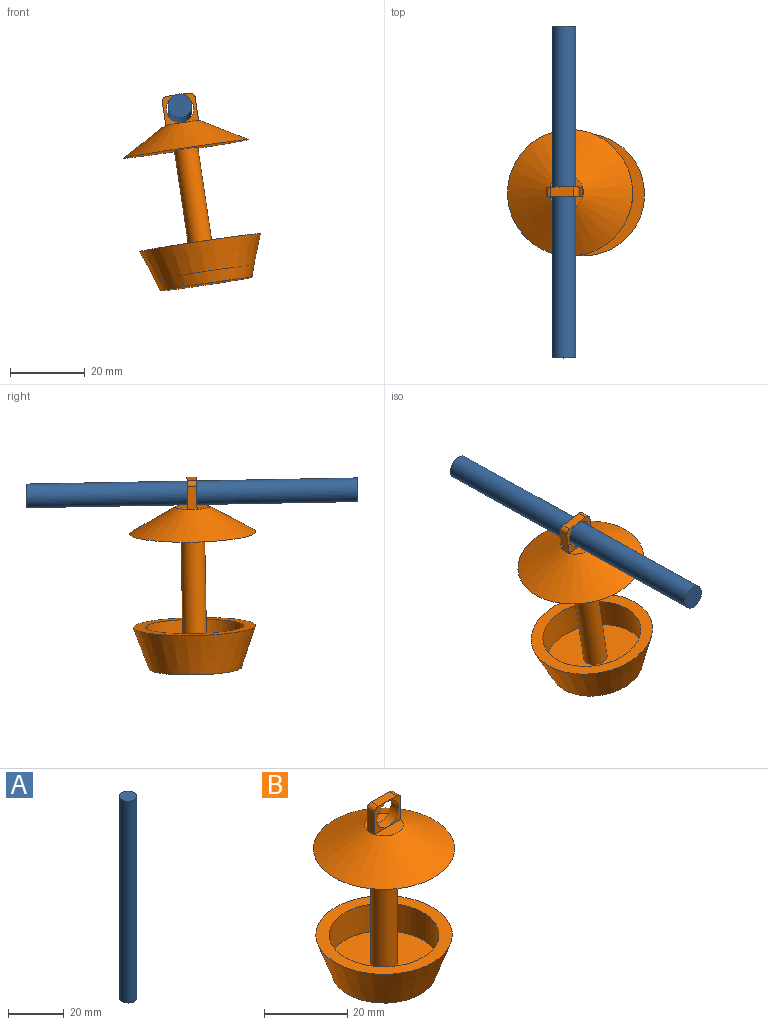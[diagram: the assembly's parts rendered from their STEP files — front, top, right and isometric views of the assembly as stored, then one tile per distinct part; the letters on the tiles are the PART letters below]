
ASSEMBLY  parts=2 mates=1
PART A: 3 faces, bbox 6.4x6.4x88.9 mm
  f0: cylinder r=3.17mm len=88.9mm, axis (0,0,-1), area 1773.5mm2, adj f1,f2
  f1: plane 6.35x6.35mm, normal (0,0,1), area 31.7mm2, adj f0
  f2: plane 6.35x6.35mm, normal (0,0,-1), area 31.7mm2, adj f0
PART B: 17 faces, bbox 33.9x33.9x51.3 mm
  f0: plane 9.29x9.29mm, normal (0,0,1), area 45.1mm2, adj f8,f9,f10,f11,f12
  f1: plane 24.77x24.77mm, normal (0,0,-1), area 481.9mm2, adj f2
  f2: cone r=16.39mm half-angle=19.6deg, axis (0,0,1), area 1081.6mm2, adj f1,f3
  f3: plane 32.78x32.78mm, normal (0,0,1), area 295.3mm2, adj f2,f4
  f4: cylinder r=13.22mm len=26.43mm, axis (0,0,1), area 672.5mm2, adj f3,f5
  f5: plane 26.43x26.43mm, normal (0,0,1), area 517mm2, adj f4,f6
  f6: cylinder r=3.17mm len=33.5mm, axis (0,0,1), area 668.3mm2, adj f5,f7
  f7: plane 33.91x33.91mm, normal (0,0,-1), area 871.3mm2, adj f6,f8
  f8: cone r=16.95mm half-angle=60.3deg, axis (0,0,-1), area 961.8mm2, adj f0,f7
  f9: plane 6.25x2.54mm, normal (1,0,0), area 15.9mm2, adj f0,f10,f12,f16
  f10: plane 8.89x7.62mm, normal (0,1,0), area 24.3mm2, adj f0,f9,f11,f13,f14,f15,f16
  f11: plane 6.25x2.54mm, normal (-1,0,0), area 15.9mm2, adj f0,f10,f12,f15
  f12: plane 8.89x7.62mm, normal (0,-1,0), area 24.3mm2, adj f0,f9,f11,f13,f14,f15,f16
  f13: plane 6.15x2.54mm, normal (0,0,1), area 15.6mm2, adj f10,f12,f15,f16
  f14: cylinder r=3.68mm len=7.37mm, axis (0,-1,0), area 58.8mm2, adj f10,f12
  f15: cylinder r=1.37mm len=2.54mm, axis (0,1,0), area 5.5mm2, adj f10,f11,f12,f13
  f16: cylinder r=1.37mm len=2.54mm, axis (0,-1,0), area 5.5mm2, adj f9,f10,f12,f13
PLACE A rot(axis=(-1,0,0),91.1deg) t=(-8.57,-59.57,50.7)mm fixed
PLACE B rot(axis=(-0.12,-0.99,0.01),8.5deg) t=(-3.23,-15.79,14.03)mm
MATE revolute B.f14 <-> A.f0  axis (0,-1,0.02) through (-8.57,-15.13,49.88)mm
